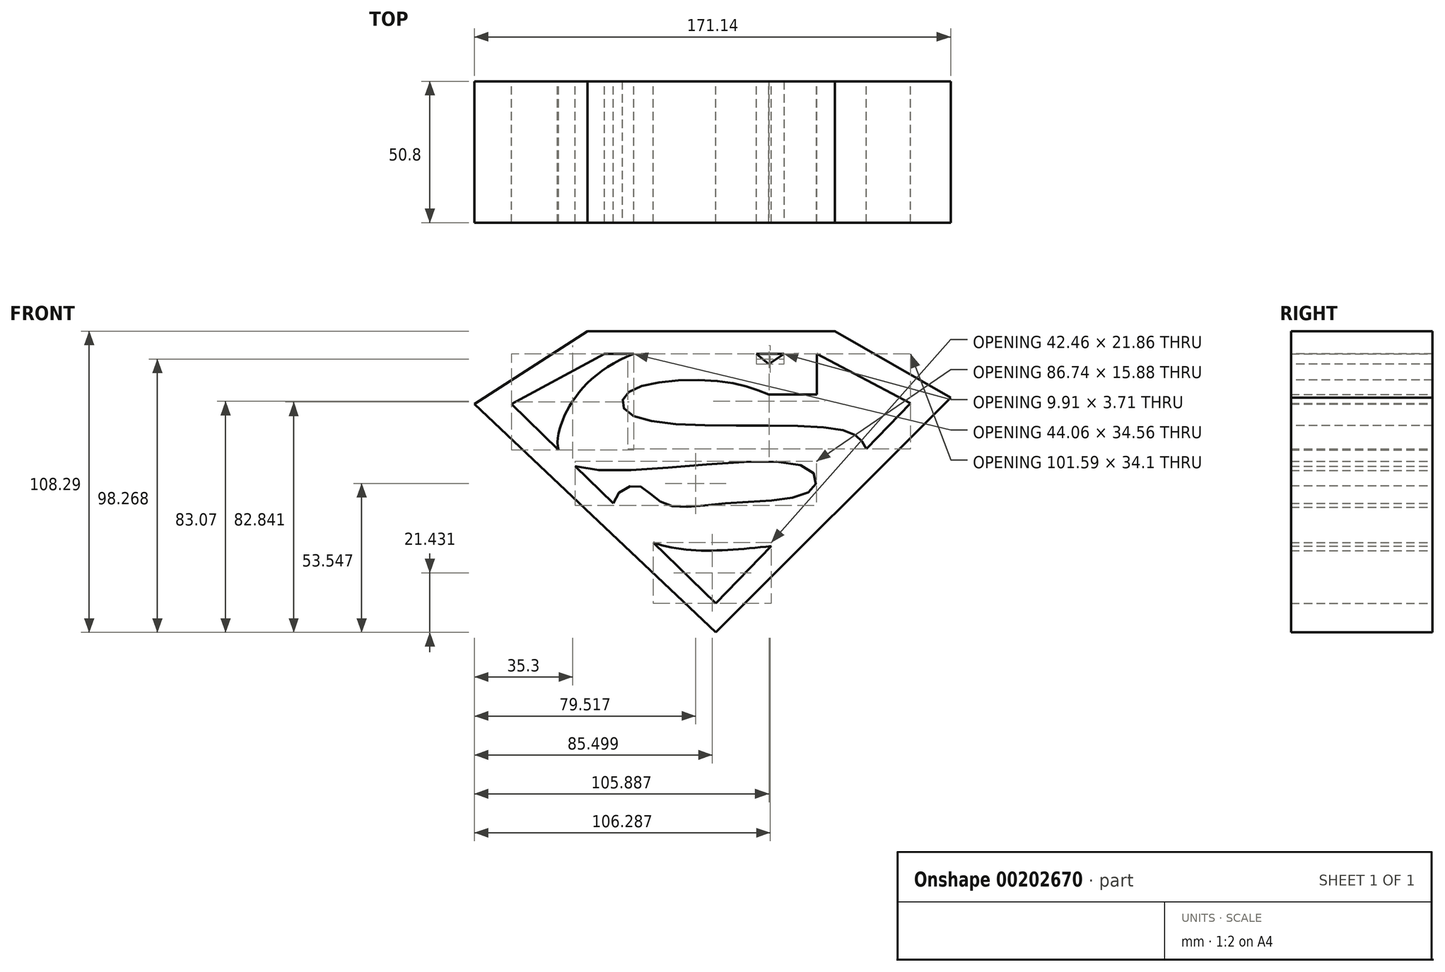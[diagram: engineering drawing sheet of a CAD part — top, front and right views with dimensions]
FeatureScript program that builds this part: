
annotation { "Feature Type Name" : "Feature", "Feature Type Description" : "" }
export const myFeature = defineFeature(function(context is Context, id is Id, definition is map)
    precondition{}
    {
        {
            var Q0;
            Q0=qCreatedBy(makeId("Front.planeOp"),FACE);
            var sketch = newSketch(context, id + "F0", { "sketchPlane" : qUnion([Q0])});
            skLineSegment(sketch, "E0", {"start": v(-39.93, 40.36) * mm, "end": v(-29.38, 40.36) * mm});
            skLineSegment(sketch, "E1", {"start": v(36.3, 40.36) * mm, "end": v(69.97, 22.56) * mm});
            skLineSegment(sketch, "E2", {"start": v(69.97, 22.56) * mm, "end": v(54.09, 6.26) * mm});
            skLineSegment(sketch, "E3", {"start": v(0, -49.26) * mm, "end": v(-22.44, -27.4) * mm});
            skLineSegment(sketch, "E4", {"start": v(-73.44, 22.29) * mm, "end": v(-39.93, 40.36) * mm});
            skFitSpline(sketch, "E5", {"points": [v(36.3, 40.36) * mm, v(36.3, 25.81) * mm], "startDerivative": vector(0, -14.56) * mm, "endDerivative": vector(0, -14.56) * mm});
            skFitSpline(sketch, "E6", {"points": [v(36.3, 25.81) * mm, v(19.11, 25.81) * mm], "startDerivative": vector(-17.18, 0) * mm, "endDerivative": vector(-17.18, 0) * mm});
            skFitSpline(sketch, "E7", {"points": [v(19.11, 25.81) * mm, v(0, 30.66) * mm, v(-32.23, 25.81) * mm, v(-29.67, 18.11) * mm, v(45.64, 12.98) * mm, v(54.09, 6.26) * mm], "startDerivative": vector(-88.8, 34.4) * mm, "endDerivative": vector(29.98, -60.48) * mm});
            skFitSpline(sketch, "E8", {"points": [v(24.53, 40.36) * mm, v(19.11, 36.65) * mm], "startDerivative": vector(-5.42, -3.72) * mm, "endDerivative": vector(-5.42, -3.72) * mm});
            skPoint(sketch, "E9.4.internal.snap0", {"position": v(34.99, -13.35) * mm});
            skPoint(sketch, "E9.5.internal.snap0", {"position": v(34.99, -13.35) * mm});
            skPoint(sketch, "E9.6.internal.snap0", {"position": v(34.99, -13.35) * mm});
            skPoint(sketch, "E9.8.internal.snap0", {"position": v(34.99, -13.35) * mm});
            skFitSpline(sketch, "E9", {"points": [v(-29.38, 40.36) * mm, v(-55.9, 13.83) * mm, v(-50.56, 0) * mm, v(31.66, 0) * mm, v(34.99, -8.13) * mm, v(3.42, -13.35) * mm, v(-18.83, -13.35) * mm, v(-28.52, -6.99) * mm, v(-36.86, -13.35) * mm, v(-22.44, -27.4) * mm, v(20.02, -28.71) * mm], "startDerivative": vector(-380.06, -144.74) * mm, "endDerivative": vector(349.52, 36.47) * mm});
            skFitSpline(sketch, "E10.trimOffspring", {"points": [v(-29.38, 40.36) * mm, v(-55.9, 13.83) * mm, v(-50.56, 0) * mm, v(31.66, 0) * mm, v(34.99, -8.13) * mm, v(3.42, -13.35) * mm, v(-18.83, -13.35) * mm, v(-28.52, -6.99) * mm, v(-36.86, -13.35) * mm, v(-22.44, -27.4) * mm, v(20.02, -28.71) * mm], "startDerivative": vector(-380.06, -144.74) * mm, "endDerivative": vector(349.52, 36.47) * mm});
            skLineSegment(sketch, "E11", {"start": v(19.11, 36.65) * mm, "end": v(14.62, 40.36) * mm});
            skLineSegment(sketch, "E12.trimOffspring", {"start": v(14.62, 40.36) * mm, "end": v(24.53, 40.36) * mm});
            skLineSegment(sketch, "E13.trimOffspring", {"start": v(-56.51, 5.8) * mm, "end": v(-73.44, 22.29) * mm});
            skLineSegment(sketch, "E14.trimOffspring", {"start": v(-36.86, -13.35) * mm, "end": v(-50.56, 0) * mm});
            skLineSegment(sketch, "E15.trimOffspring", {"start": v(20.02, -28.71) * mm, "end": v(0, -49.26) * mm});
            skLineSegment(sketch, "E16", {"start": v(-46.1, 48.53) * mm, "end": v(42.81, 48.53) * mm});
            skLineSegment(sketch, "E17", {"start": v(42.81, 48.53) * mm, "end": v(84.43, 24.67) * mm});
            skLineSegment(sketch, "E18", {"start": v(84.43, 24.67) * mm, "end": v(0, -59.76) * mm});
            skLineSegment(sketch, "E19", {"start": v(0, -59.76) * mm, "end": v(-86.71, 22.4) * mm});
            skLineSegment(sketch, "E20", {"start": v(-86.71, 22.4) * mm, "end": v(-46.1, 48.53) * mm});
            skSolve(sketch);
        }
        {
            var Q0;
            Q0=makeQuery(id+"F0.imprint","IMPRINT",FACE,{"disambiguationData":[TD([[makeQuery(id+"F0.imprint","IMPRINT",EDGE,{"derivedFrom":sQuery(id+"F0.wireOp",EDGE,"E0")}),1.0]])]});
            extrude(context, id + "F1", {"entities" : qUnion([Q0]), "depth" : 50.8 * mm});
        }
    });
